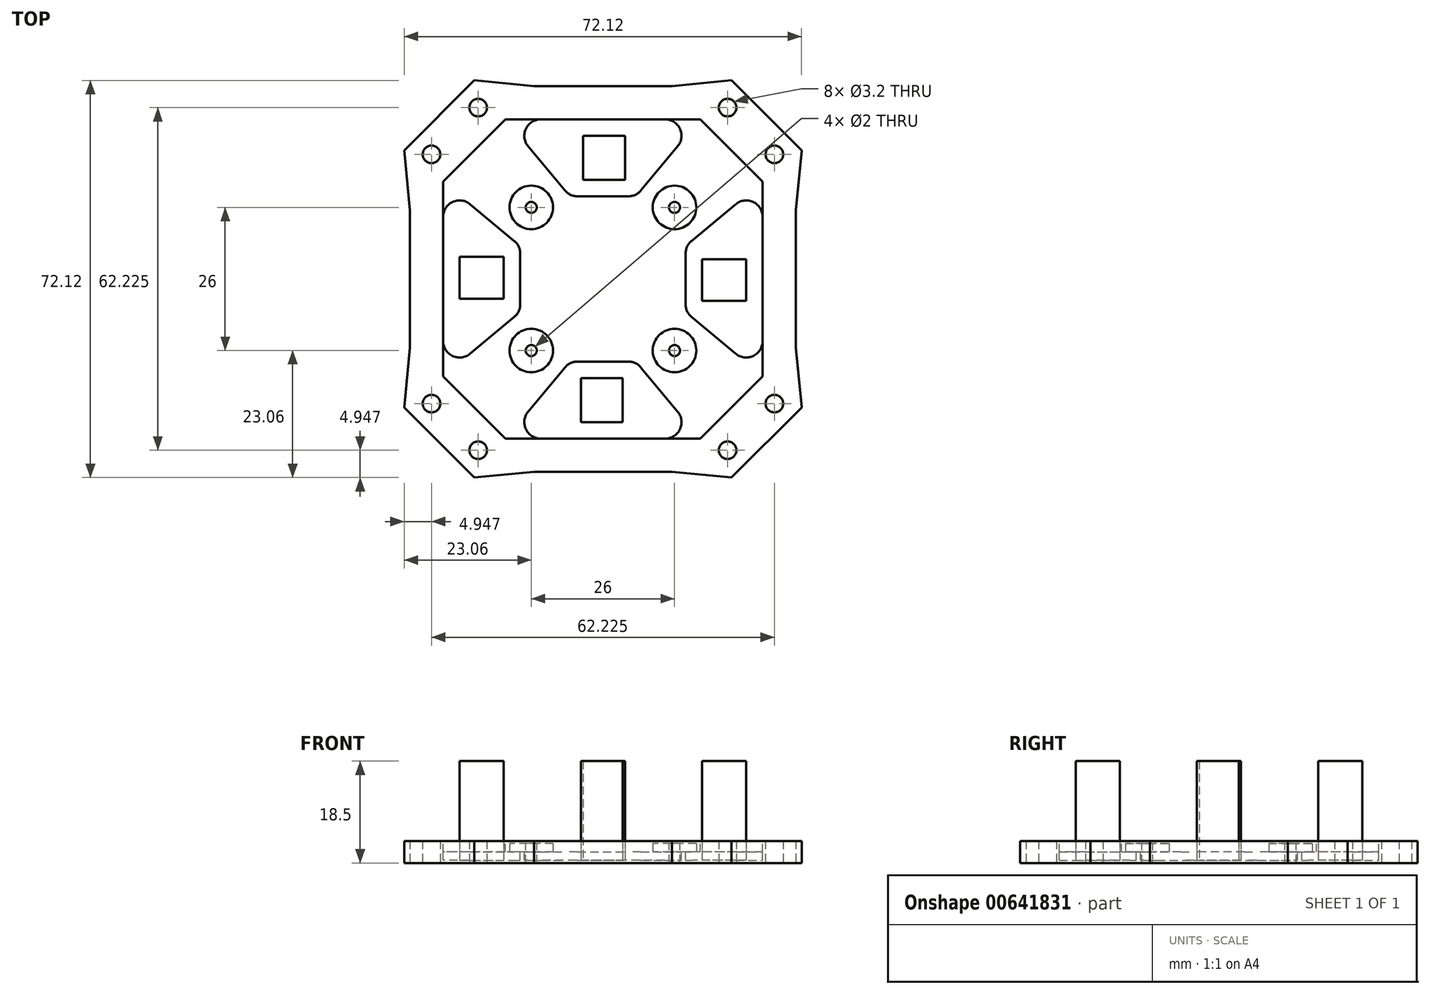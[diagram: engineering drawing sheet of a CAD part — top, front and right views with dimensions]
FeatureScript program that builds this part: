
annotation { "Feature Type Name" : "Feature", "Feature Type Description" : "" }
export const myFeature = defineFeature(function(context is Context, id is Id, definition is map)
    precondition{}
    {
        {
            var Q0;
            Q0=qCreatedBy(makeId("Top.planeOp"),FACE);
            var sketch = newSketch(context, id + "F0", { "sketchPlane" : qUnion([Q0])});
            skPoint(sketch, "E0.middle", {"position": v(0, 0) * mm});
            skLineSegment(sketch, "E1", {"start": v(0, 0) * mm, "end": v(84.85, 84.85) * mm});
            skLineSegment(sketch, "E2", {"start": v(0, 35) * mm, "end": v(0, -35) * mm});
            skLineSegment(sketch, "E3", {"start": v(-12.5, 35) * mm, "end": v(12.5, 35) * mm});
            skLineSegment(sketch, "E4.1.0", {"start": v(-35, -12.5) * mm, "end": v(-35, 12.5) * mm});
            skLineSegment(sketch, "E4.2.0", {"start": v(12.5, -35) * mm, "end": v(-12.5, -35) * mm});
            skLineSegment(sketch, "E4.3.0", {"start": v(35, 12.5) * mm, "end": v(35, -12.5) * mm});
            skLineSegment(sketch, "E5", {"start": v(20.5, 33.23) * mm, "end": v(33.23, 20.5) * mm});
            skLineSegment(sketch, "E6", {"start": v(23.33, 36.06) * mm, "end": v(36.06, 23.33) * mm});
            skLineSegment(sketch, "E7", {"start": v(12.5, 35) * mm, "end": v(23.33, 36.06) * mm});
            skLineSegment(sketch, "E8", {"start": v(35, 12.5) * mm, "end": v(36.06, 23.33) * mm});
            skCircle(sketch, "E9", {"center": v(22.63, 31.11) * mm, "radius": 1.6 * mm});
            skCircle(sketch, "E10", {"center": v(31.11, 22.63) * mm, "radius": 1.6 * mm});
            skLineSegment(sketch, "E11.1.0", {"start": v(-35, 12.5) * mm, "end": v(-36.06, 23.33) * mm});
            skLineSegment(sketch, "E11.1.1", {"start": v(-36.06, 23.33) * mm, "end": v(-23.33, 36.06) * mm});
            skCircle(sketch, "E11.1.2", {"center": v(-22.63, 31.11) * mm, "radius": 1.6 * mm});
            skCircle(sketch, "E11.1.3", {"center": v(-31.11, 22.63) * mm, "radius": 1.6 * mm});
            skLineSegment(sketch, "E11.1.4", {"start": v(-12.5, 35) * mm, "end": v(-23.33, 36.06) * mm});
            skLineSegment(sketch, "E11.2.0", {"start": v(-12.5, -35) * mm, "end": v(-23.33, -36.06) * mm});
            skLineSegment(sketch, "E11.2.1", {"start": v(-23.33, -36.06) * mm, "end": v(-36.06, -23.33) * mm});
            skCircle(sketch, "E11.2.2", {"center": v(-31.11, -22.63) * mm, "radius": 1.6 * mm});
            skCircle(sketch, "E11.2.3", {"center": v(-22.63, -31.11) * mm, "radius": 1.6 * mm});
            skLineSegment(sketch, "E11.2.4", {"start": v(-35, -12.5) * mm, "end": v(-36.06, -23.33) * mm});
            skLineSegment(sketch, "E11.3.0", {"start": v(35, -12.5) * mm, "end": v(36.06, -23.33) * mm});
            skLineSegment(sketch, "E11.3.1", {"start": v(36.06, -23.33) * mm, "end": v(23.33, -36.06) * mm});
            skCircle(sketch, "E11.3.2", {"center": v(22.63, -31.11) * mm, "radius": 1.6 * mm});
            skCircle(sketch, "E11.3.3", {"center": v(31.11, -22.63) * mm, "radius": 1.6 * mm});
            skLineSegment(sketch, "E11.3.4", {"start": v(12.5, -35) * mm, "end": v(23.33, -36.06) * mm});
            skSolve(sketch);
        }
        {
            var Q0;
            Q0 = qSketchRegion(id + "F0", true);
            extrude(context, id + "F1", {"entities" : qUnion([Q0]), "depth" : 4 * mm, "offsetDistance" : 25 * mm});
        }
        {
            var Q0;
            Q0=makeQuery(id+"F1.opExtrude","CAP_FACE",FACE,{"disambiguationData":[OSD([sQuery(id+"F0.wireOp",EDGE,"E3"),sQuery(id+"F0.wireOp",EDGE,"E4.1.0"),sQuery(id+"F0.wireOp",EDGE,"E4.2.0"),sQuery(id+"F0.wireOp",EDGE,"E4.3.0"),sQuery(id+"F0.wireOp",EDGE,"E6"),sQuery(id+"F0.wireOp",EDGE,"E7"),sQuery(id+"F0.wireOp",EDGE,"E8"),sQuery(id+"F0.wireOp",EDGE,"E9"),sQuery(id+"F0.wireOp",EDGE,"E10"),sQuery(id+"F0.wireOp",EDGE,"E11.1.0"),sQuery(id+"F0.wireOp",EDGE,"E11.1.1"),sQuery(id+"F0.wireOp",EDGE,"E11.1.2"),sQuery(id+"F0.wireOp",EDGE,"E11.1.3"),sQuery(id+"F0.wireOp",EDGE,"E11.1.4"),sQuery(id+"F0.wireOp",EDGE,"E11.2.0"),sQuery(id+"F0.wireOp",EDGE,"E11.2.1"),sQuery(id+"F0.wireOp",EDGE,"E11.2.2"),sQuery(id+"F0.wireOp",EDGE,"E11.2.3"),sQuery(id+"F0.wireOp",EDGE,"E11.2.4"),sQuery(id+"F0.wireOp",EDGE,"E11.3.0"),sQuery(id+"F0.wireOp",EDGE,"E11.3.1"),sQuery(id+"F0.wireOp",EDGE,"E11.3.2"),sQuery(id+"F0.wireOp",EDGE,"E11.3.3"),sQuery(id+"F0.wireOp",EDGE,"E11.3.4")])],"isStart":false});
            var sketch = newSketch(context, id + "F2", { "sketchPlane" : qUnion([Q0])});
            skLineSegment(sketch, "E12", {"start": v(-35, 0) * mm, "end": v(0, 0) * mm});
            skLineSegment(sketch, "E13", {"start": v(0, 0) * mm, "end": v(0, 35) * mm});
            skLineSegment(sketch, "E14", {"start": v(-17.67, 29) * mm, "end": v(17.67, 29) * mm});
            skLineSegment(sketch, "E15", {"start": v(17.67, 29) * mm, "end": v(29, 17.67) * mm});
            skLineSegment(sketch, "E16", {"start": v(29, 17.67) * mm, "end": v(29, -17.67) * mm});
            skLineSegment(sketch, "E17", {"start": v(29, -17.67) * mm, "end": v(17.67, -29) * mm});
            skLineSegment(sketch, "E18", {"start": v(17.67, -29) * mm, "end": v(-17.67, -29) * mm});
            skLineSegment(sketch, "E19", {"start": v(-17.67, -29) * mm, "end": v(-29, -17.67) * mm});
            skLineSegment(sketch, "E20", {"start": v(-29, -17.67) * mm, "end": v(-29, 17.67) * mm});
            skLineSegment(sketch, "E21", {"start": v(-29, 17.67) * mm, "end": v(-17.67, 29) * mm});
            skSolve(sketch);
        }
        {
            var Q0;
            Q0 = qSketchRegion(id + "F2", true);
            extrude(context, id + "F3", {"entities" : qUnion([Q0]), "operationType" : NewBodyOperationType.REMOVE, "oppositeDirection" : true, "depth" : 2 * mm, "offsetDistance" : 25 * mm});
        }
        {
            var Q0;
            Q0=makeQuery(id+"F3.boolean.opBoolean","COPY",FACE,{"derivedFrom":makeQuery(id+"F3.opExtrude","CAP_FACE",FACE,{"disambiguationData":[OSD([sQuery(id+"F2.wireOp",EDGE,"E14"),sQuery(id+"F2.wireOp",EDGE,"E15"),sQuery(id+"F2.wireOp",EDGE,"E16"),sQuery(id+"F2.wireOp",EDGE,"E17"),sQuery(id+"F2.wireOp",EDGE,"E18"),sQuery(id+"F2.wireOp",EDGE,"E19"),sQuery(id+"F2.wireOp",EDGE,"E20"),sQuery(id+"F2.wireOp",EDGE,"E21")])],"isStart":false})});
            var sketch = newSketch(context, id + "F4", { "sketchPlane" : qUnion([Q0])});
            skLineSegment(sketch, "E22", {"start": v(0, 29) * mm, "end": v(0, 0) * mm});
            skLineSegment(sketch, "E23", {"start": v(0, 0) * mm, "end": v(-29, 0) * mm});
            skLineSegment(sketch, "E24", {"start": v(-24.08, 13.57) * mm, "end": v(-16.08, 6.9) * mm});
            skLineSegment(sketch, "E25", {"start": v(-15, 4.6) * mm, "end": v(-15, -4.6) * mm});
            skLineSegment(sketch, "E26", {"start": v(-16.08, -6.9) * mm, "end": v(-24.08, -13.57) * mm});
            skLineSegment(sketch, "E27", {"start": v(-29, -11.26) * mm, "end": v(-29, 11.26) * mm});
            skPoint(sketch, "E28.visualSharp", {"position": v(-15, 6) * mm});
            skArc(sketch, "E28.filletArc", {"start": v(-15, 4.6) * mm, "mid": v(-15.28, 5.87) * mm, "end": v(-16.08, 6.9) * mm});
            skPoint(sketch, "E29.visualSharp", {"position": v(-15, -6) * mm});
            skArc(sketch, "E29.filletArc", {"start": v(-16.08, -6.9) * mm, "mid": v(-15.28, -5.87) * mm, "end": v(-15, -4.6) * mm});
            skPoint(sketch, "E30.visualSharp", {"position": v(-29, -17.67) * mm});
            skArc(sketch, "E30.filletArc", {"start": v(-29, -11.26) * mm, "mid": v(-27.27, -13.98) * mm, "end": v(-24.08, -13.57) * mm});
            skPoint(sketch, "E31.visualSharp", {"position": v(-29, 17.67) * mm});
            skArc(sketch, "E31.filletArc", {"start": v(-24.08, 13.57) * mm, "mid": v(-27.27, 13.98) * mm, "end": v(-29, 11.26) * mm});
            skLineSegment(sketch, "E32.1.0", {"start": v(-13.57, -24.08) * mm, "end": v(-6.9, -16.08) * mm});
            skArc(sketch, "E32.1.1", {"start": v(-13.57, -24.08) * mm, "mid": v(-13.98, -27.27) * mm, "end": v(-11.26, -29) * mm});
            skLineSegment(sketch, "E32.1.2", {"start": v(0, 0) * mm, "end": v(0, -29) * mm});
            skLineSegment(sketch, "E32.1.3", {"start": v(6.9, -16.08) * mm, "end": v(13.57, -24.08) * mm});
            skArc(sketch, "E32.1.4", {"start": v(11.26, -29) * mm, "mid": v(13.98, -27.27) * mm, "end": v(13.57, -24.08) * mm});
            skLineSegment(sketch, "E32.1.5", {"start": v(-4.6, -15) * mm, "end": v(4.6, -15) * mm});
            skArc(sketch, "E32.1.6", {"start": v(6.9, -16.08) * mm, "mid": v(5.87, -15.28) * mm, "end": v(4.6, -15) * mm});
            skArc(sketch, "E32.1.7", {"start": v(-4.6, -15) * mm, "mid": v(-5.87, -15.28) * mm, "end": v(-6.9, -16.08) * mm});
            skLineSegment(sketch, "E32.2.0", {"start": v(24.08, -13.57) * mm, "end": v(16.08, -6.9) * mm});
            skArc(sketch, "E32.2.1", {"start": v(24.08, -13.57) * mm, "mid": v(27.27, -13.98) * mm, "end": v(29, -11.26) * mm});
            skLineSegment(sketch, "E32.2.2", {"start": v(0, 0) * mm, "end": v(29, 0) * mm});
            skLineSegment(sketch, "E32.2.3", {"start": v(16.08, 6.9) * mm, "end": v(24.08, 13.57) * mm});
            skArc(sketch, "E32.2.4", {"start": v(29, 11.26) * mm, "mid": v(27.27, 13.98) * mm, "end": v(24.08, 13.57) * mm});
            skLineSegment(sketch, "E32.2.5", {"start": v(15, -4.6) * mm, "end": v(15, 4.6) * mm});
            skArc(sketch, "E32.2.6", {"start": v(16.08, 6.9) * mm, "mid": v(15.28, 5.87) * mm, "end": v(15, 4.6) * mm});
            skArc(sketch, "E32.2.7", {"start": v(15, -4.6) * mm, "mid": v(15.28, -5.87) * mm, "end": v(16.08, -6.9) * mm});
            skLineSegment(sketch, "E32.3.0", {"start": v(13.57, 24.08) * mm, "end": v(6.9, 16.08) * mm});
            skArc(sketch, "E32.3.1", {"start": v(13.57, 24.08) * mm, "mid": v(13.98, 27.27) * mm, "end": v(11.26, 29) * mm});
            skLineSegment(sketch, "E32.3.2", {"start": v(0, 0) * mm, "end": v(0, 29) * mm});
            skLineSegment(sketch, "E32.3.3", {"start": v(-6.9, 16.08) * mm, "end": v(-13.57, 24.08) * mm});
            skArc(sketch, "E32.3.4", {"start": v(-11.26, 29) * mm, "mid": v(-13.98, 27.27) * mm, "end": v(-13.57, 24.08) * mm});
            skLineSegment(sketch, "E32.3.5", {"start": v(4.6, 15) * mm, "end": v(-4.6, 15) * mm});
            skArc(sketch, "E32.3.6", {"start": v(-6.9, 16.08) * mm, "mid": v(-5.87, 15.28) * mm, "end": v(-4.6, 15) * mm});
            skArc(sketch, "E32.3.7", {"start": v(4.6, 15) * mm, "mid": v(5.87, 15.28) * mm, "end": v(6.9, 16.08) * mm});
            skPoint(sketch, "E32.center", {"position": v(0, 0) * mm});
            skSolve(sketch);
        }
        {
            var Q0;
            Q0 = qSketchRegion(id + "F4", true);
            var Q1;
            Q1=makeQuery(id+"F4.imprint","IMPRINT",FACE,{"disambiguationData":[TD([[makeQuery(id+"F4.imprint","IMPRINT",EDGE,{"derivedFrom":sQuery(id+"F4.wireOp",EDGE,"E32.3.3")}),-1.0]])]});
            var Q2;
            Q2=makeQuery(id+"F4.imprint","IMPRINT",FACE,{"disambiguationData":[TD([[makeQuery(id+"F4.imprint","IMPRINT",EDGE,{"derivedFrom":sQuery(id+"F4.wireOp",EDGE,"E32.3.0")}),-1.0]])]});
            var Q3;
            Q3=makeQuery(id+"F4.imprint","IMPRINT",FACE,{"disambiguationData":[TD([[makeQuery(id+"F4.imprint","IMPRINT",EDGE,{"derivedFrom":sQuery(id+"F4.wireOp",EDGE,"E32.2.3")}),-1.0]])]});
            var Q4;
            Q4=makeQuery(id+"F4.imprint","IMPRINT",FACE,{"disambiguationData":[TD([[makeQuery(id+"F4.imprint","IMPRINT",EDGE,{"derivedFrom":sQuery(id+"F4.wireOp",EDGE,"E32.2.0")}),-1.0]])]});
            var Q5;
            Q5=makeQuery(id+"F4.imprint","IMPRINT",FACE,{"disambiguationData":[TD([[makeQuery(id+"F4.imprint","IMPRINT",EDGE,{"derivedFrom":sQuery(id+"F4.wireOp",EDGE,"E32.1.3")}),-1.0]])]});
            var Q6;
            Q6=makeQuery(id+"F4.imprint","IMPRINT",FACE,{"disambiguationData":[TD([[makeQuery(id+"F4.imprint","IMPRINT",EDGE,{"derivedFrom":sQuery(id+"F4.wireOp",EDGE,"E32.1.0")}),-1.0]])]});
            extrude(context, id + "F5", {"entities" : qUnion([Q0, Q1, Q2, Q3, Q4, Q5, Q6]), "operationType" : NewBodyOperationType.REMOVE, "oppositeDirection" : true, "depth" : 1.5 * mm, "offsetDistance" : 25 * mm});
        }
        {
            var Q0;
            Q0=makeQuery(id+"F3.boolean.opBoolean","COPY",FACE,{"derivedFrom":makeQuery(id+"F3.opExtrude","CAP_FACE",FACE,{"disambiguationData":[OSD([sQuery(id+"F2.wireOp",EDGE,"E14"),sQuery(id+"F2.wireOp",EDGE,"E15"),sQuery(id+"F2.wireOp",EDGE,"E16"),sQuery(id+"F2.wireOp",EDGE,"E17"),sQuery(id+"F2.wireOp",EDGE,"E18"),sQuery(id+"F2.wireOp",EDGE,"E19"),sQuery(id+"F2.wireOp",EDGE,"E20"),sQuery(id+"F2.wireOp",EDGE,"E21")])],"isStart":false})});
            var sketch = newSketch(context, id + "F6", { "sketchPlane" : qUnion([Q0])});
            skLineSegment(sketch, "E33.bottom", {"start": v(0, 0) * mm, "end": v(13, 0) * mm});
            skLineSegment(sketch, "E33.top", {"start": v(0, 13) * mm, "end": v(13, 13) * mm});
            skLineSegment(sketch, "E33.left", {"start": v(0, 0) * mm, "end": v(0, 13) * mm});
            skLineSegment(sketch, "E33.right", {"start": v(13, 0) * mm, "end": v(13, 13) * mm});
            skCircle(sketch, "E34", {"center": v(13, 13) * mm, "radius": 1 * mm});
            skLineSegment(sketch, "E35.top", {"start": v(0, -13) * mm, "end": v(13, -13) * mm});
            skLineSegment(sketch, "E35.left", {"start": v(0, 0) * mm, "end": v(0, -13) * mm});
            skLineSegment(sketch, "E35.right", {"start": v(13, 0) * mm, "end": v(13, -13) * mm});
            skLineSegment(sketch, "E36.bottom", {"start": v(0, 0) * mm, "end": v(-13, 0) * mm});
            skLineSegment(sketch, "E36.top", {"start": v(0, -13) * mm, "end": v(-13, -13) * mm});
            skLineSegment(sketch, "E36.right", {"start": v(-13, 0) * mm, "end": v(-13, -13) * mm});
            skLineSegment(sketch, "E37.top", {"start": v(0, 13) * mm, "end": v(-13, 13) * mm});
            skLineSegment(sketch, "E37.right", {"start": v(-13, 0) * mm, "end": v(-13, 13) * mm});
            skCircle(sketch, "E38", {"center": v(-13, 13) * mm, "radius": 1 * mm});
            skCircle(sketch, "E39", {"center": v(-13, -13) * mm, "radius": 1 * mm});
            skCircle(sketch, "E40", {"center": v(13, -13) * mm, "radius": 1 * mm});
            skCircle(sketch, "E41", {"center": v(-13, 13) * mm, "radius": 3.95 * mm});
            skCircle(sketch, "E42", {"center": v(-13, -13) * mm, "radius": 3.95 * mm});
            skCircle(sketch, "E43", {"center": v(13, -13) * mm, "radius": 3.95 * mm});
            skCircle(sketch, "E44", {"center": v(13, 13) * mm, "radius": 3.95 * mm});
            skSolve(sketch);
        }
        {
            var Q0;
            {var subQ0=sQuery(id+"F6.wireOp",EDGE,"E33.right");var subQ1=sQuery(id+"F6.wireOp",EDGE,"E33.top");var subQ2=makeQuery(id+"F6.imprint","INTERSECT",VERTEX,{"derivedFrom":[subQ1,subQ0]});Q0=makeQuery(id+"F6.imprint","IMPRINT",FACE,{"disambiguationData":[TD([[makeQuery(id+"F6.imprint","IMPRINT",EDGE,{"disambiguationData":[TD([[subQ2,1.0]])],"derivedFrom":subQ1}),1.0]])]});}
            var Q1;
            {var subQ0=sQuery(id+"F6.wireOp",EDGE,"E33.right");var subQ1=sQuery(id+"F6.wireOp",EDGE,"E33.top");var subQ2=makeQuery(id+"F6.imprint","INTERSECT",VERTEX,{"derivedFrom":[subQ1,subQ0]});Q1=makeQuery(id+"F6.imprint","IMPRINT",FACE,{"disambiguationData":[TD([[makeQuery(id+"F6.imprint","IMPRINT",EDGE,{"disambiguationData":[TD([[subQ2,1.0]])],"derivedFrom":subQ1}),-1.0]])]});}
            extrude(context, id + "F7", {"entities" : qUnion([Q0, Q1]), "operationType" : NewBodyOperationType.REMOVE, "endBound" : BoundingType.THROUGH_ALL, "oppositeDirection" : true, "depth" : 25 * mm, "offsetDistance" : 25 * mm});
        }
        {
            var Q0;
            Q0 = qSketchRegion(id + "F6", true);
            extrude(context, id + "F8", {"entities" : qUnion([Q0]), "operationType" : NewBodyOperationType.REMOVE, "depth" : 25 * mm, "offsetDistance" : 25 * mm});
        }
        {
            var Q0;
            {var subQ0=sQuery(id+"F6.wireOp",EDGE,"E37.right");var subQ1=sQuery(id+"F6.wireOp",EDGE,"E37.top");var subQ2=makeQuery(id+"F6.imprint","INTERSECT",VERTEX,{"derivedFrom":[subQ1,subQ0]});Q0=makeQuery(id+"F6.imprint","IMPRINT",FACE,{"disambiguationData":[TD([[makeQuery(id+"F6.imprint","IMPRINT",EDGE,{"disambiguationData":[TD([[subQ2,1.0]])],"derivedFrom":subQ1}),-1.0]])]});}
            var Q1;
            {var subQ0=sQuery(id+"F6.wireOp",EDGE,"E37.right");var subQ1=sQuery(id+"F6.wireOp",EDGE,"E37.top");var subQ2=makeQuery(id+"F6.imprint","INTERSECT",VERTEX,{"derivedFrom":[subQ1,subQ0]});Q1=makeQuery(id+"F6.imprint","IMPRINT",FACE,{"disambiguationData":[TD([[makeQuery(id+"F6.imprint","IMPRINT",EDGE,{"disambiguationData":[TD([[subQ2,1.0]])],"derivedFrom":subQ1}),1.0]])]});}
            var Q2;
            {var subQ0=sQuery(id+"F6.wireOp",EDGE,"E36.right");var subQ1=sQuery(id+"F6.wireOp",EDGE,"E36.top");var subQ2=makeQuery(id+"F6.imprint","INTERSECT",VERTEX,{"derivedFrom":[subQ1,subQ0]});Q2=makeQuery(id+"F6.imprint","IMPRINT",FACE,{"disambiguationData":[TD([[makeQuery(id+"F6.imprint","IMPRINT",EDGE,{"disambiguationData":[TD([[subQ2,1.0]])],"derivedFrom":subQ1}),1.0]])]});}
            var Q3;
            {var subQ0=sQuery(id+"F6.wireOp",EDGE,"E36.right");var subQ1=sQuery(id+"F6.wireOp",EDGE,"E36.top");var subQ2=makeQuery(id+"F6.imprint","INTERSECT",VERTEX,{"derivedFrom":[subQ1,subQ0]});Q3=makeQuery(id+"F6.imprint","IMPRINT",FACE,{"disambiguationData":[TD([[makeQuery(id+"F6.imprint","IMPRINT",EDGE,{"disambiguationData":[TD([[subQ2,1.0]])],"derivedFrom":subQ1}),-1.0]])]});}
            var Q4;
            {var subQ0=sQuery(id+"F6.wireOp",EDGE,"E35.right");var subQ1=sQuery(id+"F6.wireOp",EDGE,"E35.top");var subQ2=makeQuery(id+"F6.imprint","INTERSECT",VERTEX,{"derivedFrom":[subQ1,subQ0]});Q4=makeQuery(id+"F6.imprint","IMPRINT",FACE,{"disambiguationData":[TD([[makeQuery(id+"F6.imprint","IMPRINT",EDGE,{"disambiguationData":[TD([[subQ2,1.0]])],"derivedFrom":subQ1}),-1.0]])]});}
            var Q5;
            {var subQ0=sQuery(id+"F6.wireOp",EDGE,"E35.right");var subQ1=sQuery(id+"F6.wireOp",EDGE,"E35.top");var subQ2=makeQuery(id+"F6.imprint","INTERSECT",VERTEX,{"derivedFrom":[subQ1,subQ0]});Q5=makeQuery(id+"F6.imprint","IMPRINT",FACE,{"disambiguationData":[TD([[makeQuery(id+"F6.imprint","IMPRINT",EDGE,{"disambiguationData":[TD([[subQ2,1.0]])],"derivedFrom":subQ1}),1.0]])]});}
            var Q6;
            {var subQ0=sQuery(id+"F6.wireOp",EDGE,"E33.right");var subQ1=sQuery(id+"F6.wireOp",EDGE,"E33.top");var subQ2=makeQuery(id+"F6.imprint","INTERSECT",VERTEX,{"derivedFrom":[subQ1,subQ0]});Q6=makeQuery(id+"F6.imprint","IMPRINT",FACE,{"disambiguationData":[TD([[makeQuery(id+"F6.imprint","IMPRINT",EDGE,{"disambiguationData":[TD([[subQ2,1.0]])],"derivedFrom":subQ1}),-1.0]])]});}
            var Q7;
            {var subQ0=sQuery(id+"F6.wireOp",EDGE,"E33.right");var subQ1=sQuery(id+"F6.wireOp",EDGE,"E33.top");var subQ2=makeQuery(id+"F6.imprint","INTERSECT",VERTEX,{"derivedFrom":[subQ1,subQ0]});Q7=makeQuery(id+"F6.imprint","IMPRINT",FACE,{"disambiguationData":[TD([[makeQuery(id+"F6.imprint","IMPRINT",EDGE,{"disambiguationData":[TD([[subQ2,1.0]])],"derivedFrom":subQ1}),1.0]])]});}
            extrude(context, id + "F9", {"entities" : qUnion([Q0, Q1, Q2, Q3, Q4, Q5, Q6, Q7]), "operationType" : NewBodyOperationType.REMOVE, "oppositeDirection" : true, "depth" : 25 * mm, "offsetDistance" : 25 * mm});
        }
        {
            var Q0;
            {var subQ0=sQuery(id+"F6.wireOp",EDGE,"E41");var subQ1=sQuery(id+"F6.wireOp",EDGE,"E37.top");var subQ2=makeQuery(id+"F6.imprint","INTERSECT",VERTEX,{"derivedFrom":[subQ1,subQ0]});Q0=makeQuery(id+"F6.imprint","IMPRINT",FACE,{"disambiguationData":[TD([[makeQuery(id+"F6.imprint","IMPRINT",EDGE,{"disambiguationData":[TD([[subQ2,-1.0]])],"derivedFrom":subQ1}),-1.0]])]});}
            var Q1;
            {var subQ0=sQuery(id+"F6.wireOp",EDGE,"E41");var subQ1=sQuery(id+"F6.wireOp",EDGE,"E37.top");var subQ2=makeQuery(id+"F6.imprint","INTERSECT",VERTEX,{"derivedFrom":[subQ1,subQ0]});Q1=makeQuery(id+"F6.imprint","IMPRINT",FACE,{"disambiguationData":[TD([[makeQuery(id+"F6.imprint","IMPRINT",EDGE,{"disambiguationData":[TD([[subQ2,-1.0]])],"derivedFrom":subQ1}),1.0]])]});}
            var Q2;
            {var subQ0=sQuery(id+"F6.wireOp",EDGE,"E42");var subQ1=sQuery(id+"F6.wireOp",EDGE,"E36.top");var subQ2=makeQuery(id+"F6.imprint","INTERSECT",VERTEX,{"derivedFrom":[subQ1,subQ0]});Q2=makeQuery(id+"F6.imprint","IMPRINT",FACE,{"disambiguationData":[TD([[makeQuery(id+"F6.imprint","IMPRINT",EDGE,{"disambiguationData":[TD([[subQ2,-1.0]])],"derivedFrom":subQ1}),1.0]])]});}
            var Q3;
            {var subQ0=sQuery(id+"F6.wireOp",EDGE,"E42");var subQ1=sQuery(id+"F6.wireOp",EDGE,"E36.top");var subQ2=makeQuery(id+"F6.imprint","INTERSECT",VERTEX,{"derivedFrom":[subQ1,subQ0]});Q3=makeQuery(id+"F6.imprint","IMPRINT",FACE,{"disambiguationData":[TD([[makeQuery(id+"F6.imprint","IMPRINT",EDGE,{"disambiguationData":[TD([[subQ2,-1.0]])],"derivedFrom":subQ1}),-1.0]])]});}
            var Q4;
            {var subQ0=sQuery(id+"F6.wireOp",EDGE,"E43");var subQ1=sQuery(id+"F6.wireOp",EDGE,"E35.top");var subQ2=makeQuery(id+"F6.imprint","INTERSECT",VERTEX,{"derivedFrom":[subQ1,subQ0]});Q4=makeQuery(id+"F6.imprint","IMPRINT",FACE,{"disambiguationData":[TD([[makeQuery(id+"F6.imprint","IMPRINT",EDGE,{"disambiguationData":[TD([[subQ2,-1.0]])],"derivedFrom":subQ1}),-1.0]])]});}
            var Q5;
            {var subQ0=sQuery(id+"F6.wireOp",EDGE,"E43");var subQ1=sQuery(id+"F6.wireOp",EDGE,"E35.top");var subQ2=makeQuery(id+"F6.imprint","INTERSECT",VERTEX,{"derivedFrom":[subQ1,subQ0]});Q5=makeQuery(id+"F6.imprint","IMPRINT",FACE,{"disambiguationData":[TD([[makeQuery(id+"F6.imprint","IMPRINT",EDGE,{"disambiguationData":[TD([[subQ2,-1.0]])],"derivedFrom":subQ1}),1.0]])]});}
            var Q6;
            {var subQ0=sQuery(id+"F6.wireOp",EDGE,"E44");var subQ1=sQuery(id+"F6.wireOp",EDGE,"E33.top");var subQ2=makeQuery(id+"F6.imprint","INTERSECT",VERTEX,{"derivedFrom":[subQ1,subQ0]});Q6=makeQuery(id+"F6.imprint","IMPRINT",FACE,{"disambiguationData":[TD([[makeQuery(id+"F6.imprint","IMPRINT",EDGE,{"disambiguationData":[TD([[subQ2,-1.0]])],"derivedFrom":subQ1}),1.0]])]});}
            var Q7;
            {var subQ0=sQuery(id+"F6.wireOp",EDGE,"E44");var subQ1=sQuery(id+"F6.wireOp",EDGE,"E33.top");var subQ2=makeQuery(id+"F6.imprint","INTERSECT",VERTEX,{"derivedFrom":[subQ1,subQ0]});Q7=makeQuery(id+"F6.imprint","IMPRINT",FACE,{"disambiguationData":[TD([[makeQuery(id+"F6.imprint","IMPRINT",EDGE,{"disambiguationData":[TD([[subQ2,-1.0]])],"derivedFrom":subQ1}),-1.0]])]});}
            extrude(context, id + "F10", {"entities" : qUnion([Q0, Q1, Q2, Q3, Q4, Q5, Q6, Q7]), "operationType" : NewBodyOperationType.ADD, "depth" : 1.5 * mm, "offsetDistance" : 25 * mm});
        }
        {
            var Q0;
            Q0=makeQuery(id+"F5.boolean.opBoolean","COPY",FACE,{"derivedFrom":makeQuery(id+"F5.opExtrude","CAP_FACE",FACE,{"disambiguationData":[OSD([sQuery(id+"F4.wireOp",EDGE,"E24"),sQuery(id+"F4.wireOp",EDGE,"E25"),sQuery(id+"F4.wireOp",EDGE,"E26"),sQuery(id+"F4.wireOp",EDGE,"E27"),sQuery(id+"F4.wireOp",EDGE,"E28.filletArc"),sQuery(id+"F4.wireOp",EDGE,"E29.filletArc"),sQuery(id+"F4.wireOp",EDGE,"E30.filletArc"),sQuery(id+"F4.wireOp",EDGE,"E31.filletArc")])],"isStart":false})});
            var sketch = newSketch(context, id + "F11", { "sketchPlane" : qUnion([Q0])});
            skLineSegment(sketch, "E45.bottom", {"start": v(-26, 4) * mm, "end": v(-18, 4) * mm});
            skLineSegment(sketch, "E45.top", {"start": v(-26, -3.6) * mm, "end": v(-18, -3.6) * mm});
            skLineSegment(sketch, "E45.left", {"start": v(-26, 4) * mm, "end": v(-26, -3.6) * mm});
            skLineSegment(sketch, "E45.right", {"start": v(-18, 4) * mm, "end": v(-18, -3.6) * mm});
            skLineSegment(sketch, "E46.1.0", {"start": v(-4, -26) * mm, "end": v(3.6, -26) * mm});
            skLineSegment(sketch, "E46.1.1", {"start": v(-4, -26) * mm, "end": v(-4, -18) * mm});
            skLineSegment(sketch, "E46.1.2", {"start": v(-4, -18) * mm, "end": v(3.6, -18) * mm});
            skLineSegment(sketch, "E46.1.3", {"start": v(3.6, -26) * mm, "end": v(3.6, -18) * mm});
            skLineSegment(sketch, "E46.2.0", {"start": v(26, -4) * mm, "end": v(26, 3.6) * mm});
            skLineSegment(sketch, "E46.2.1", {"start": v(26, -4) * mm, "end": v(18, -4) * mm});
            skLineSegment(sketch, "E46.2.2", {"start": v(18, -4) * mm, "end": v(18, 3.6) * mm});
            skLineSegment(sketch, "E46.2.3", {"start": v(26, 3.6) * mm, "end": v(18, 3.6) * mm});
            skLineSegment(sketch, "E46.3.0", {"start": v(4, 26) * mm, "end": v(-3.6, 26) * mm});
            skLineSegment(sketch, "E46.3.1", {"start": v(4, 26) * mm, "end": v(4, 18) * mm});
            skLineSegment(sketch, "E46.3.2", {"start": v(4, 18) * mm, "end": v(-3.6, 18) * mm});
            skLineSegment(sketch, "E46.3.3", {"start": v(-3.6, 26) * mm, "end": v(-3.6, 18) * mm});
            skPoint(sketch, "E46.center", {"position": v(0, 0) * mm});
            skSolve(sketch);
        }
        {
            var Q0;
            Q0 = qSketchRegion(id + "F11", true);
            extrude(context, id + "F12", {"entities" : qUnion([Q0]), "operationType" : NewBodyOperationType.ADD, "depth" : 18 * mm, "offsetDistance" : 25 * mm});
        }
    });
